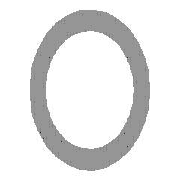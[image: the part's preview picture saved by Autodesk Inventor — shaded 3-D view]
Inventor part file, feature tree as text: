
AUTODESK INVENTOR PART (.ipt)
format: ipt  version: 2021 (Build 250183000, 183)  size: 369,664 bytes
history: native  units: mm (DEFAULTED — no unit token found)
features: other x7, plane x3, sketch x3, sweep x1, split x1
ambient origin geometry x8: Origin, YZ Plane, XZ Plane, XY Plane, X Axis, Y Axis, Z Axis, Center Point
bodies: Solid1 (feature_tree)
feature tree (15):
  parser-record x1  (decoder bookkeeping rows leaked as tree rows — omitted from the tree; the rows remain in map.json)
  other  "Driven Length"
  other  "Plano inicial"
  other  "Plano final"
  other  "Trayectoria de barrido"
  plane  "Plano de trabajo de orientación"
  sweep  "Cuerpo"
  plane  "Plano de trabajo5"
  split  "Dividir1"
  sketch  "Sketch3"  dims[d0=26.67mm d1=2.8702mm]
  plane  "Work Plane3"
  sketch  "Sketch4"  dims[d4=-0.0mm]
  sketch  "Boceto5"  dims[d5=1154.314954mm d6=90.0deg d7=1154.314954mm d8=0.0mm d9=0.0mm d10=0.0mm d11=90.0deg d12=0.0mm d13=90.0deg]
  other  "Sup1"
  other  "SuperficieSolevación1"
